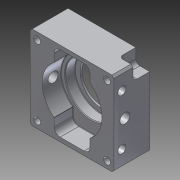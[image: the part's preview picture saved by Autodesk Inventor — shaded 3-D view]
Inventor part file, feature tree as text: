
AUTODESK INVENTOR PART (.ipt)
format: ipt  version: 2014 SP1 (Build 180222100, 222)  size: 316,416 bytes
history: native  units: in
note: dims shown in document units (in); Inventor stores cm internally (conversion verified against a paired STEP export)
features: hole x1, other x1, imported_body x1
ambient origin geometry x8: Origin, YZ Plane, XZ Plane, XY Plane, X Axis, Y Axis, Z Axis, Center Point
bodies: Body1 (feature_tree)
feature tree (3):
  hole  "Hole1"  [1 undecoded]
  other  "217-2625-001 Rev1.ipt1"
  imported_body  "Base1"
note: 1 required parameter value undecoded (feature->parameter linkage not recoverable at this tier; creation-order binding heuristic only, values carry confidence <= 0.55)
